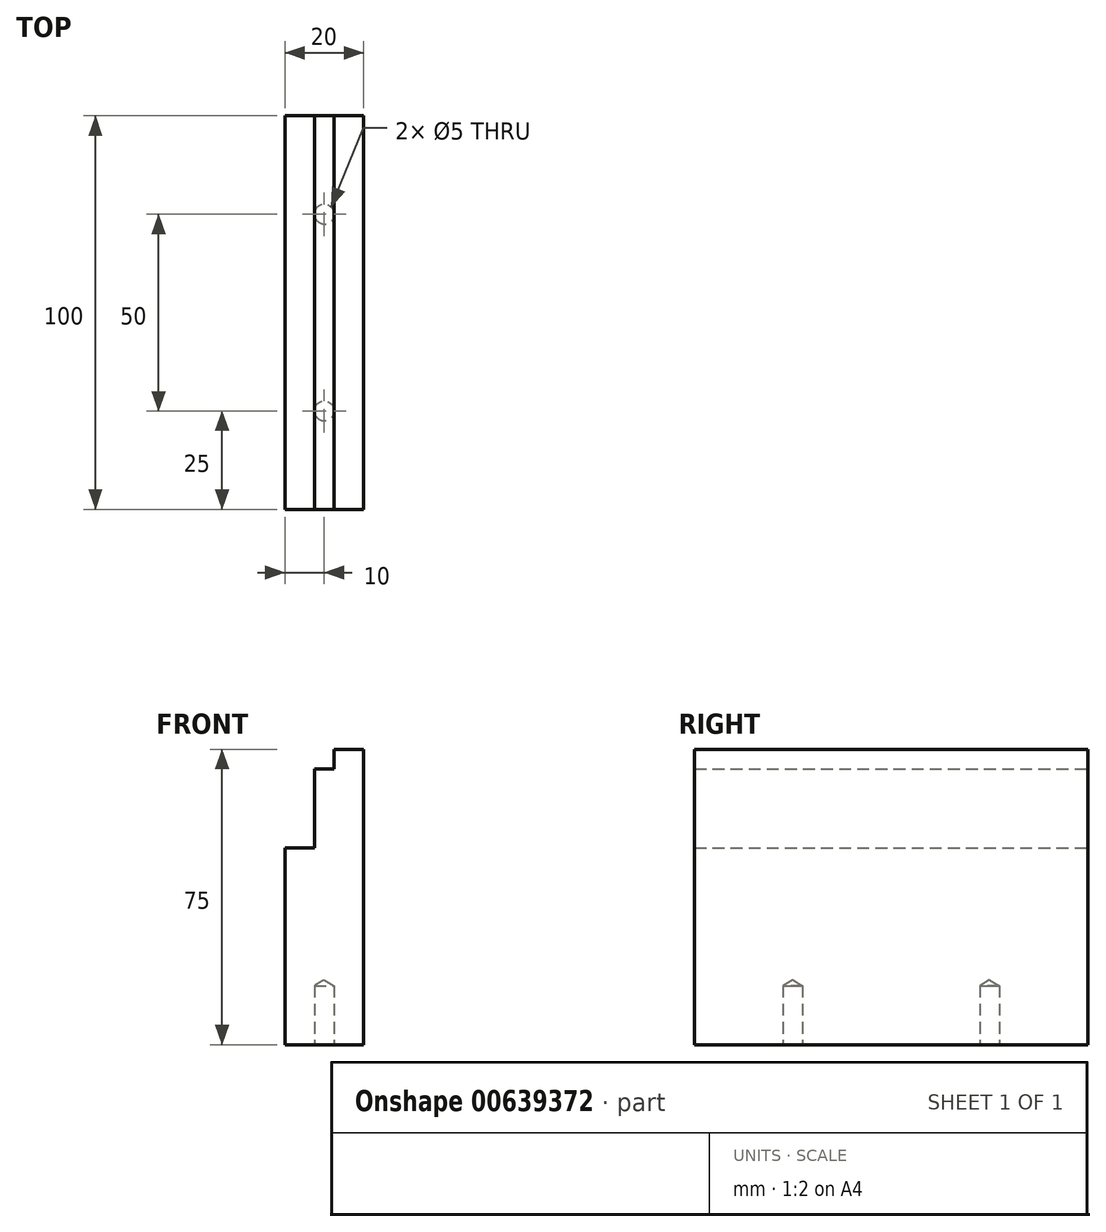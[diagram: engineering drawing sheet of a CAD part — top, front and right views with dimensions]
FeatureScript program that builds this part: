
annotation { "Feature Type Name" : "Feature", "Feature Type Description" : "" }
export const myFeature = defineFeature(function(context is Context, id is Id, definition is map)
    precondition{}
    {
        {
            var Q0;
            Q0=qCreatedBy(makeId("Front.planeOp"),FACE);
            var sketch = newSketch(context, id + "F0", { "sketchPlane" : qUnion([Q0])});
            skLineSegment(sketch, "E0.top", {"start": v(130, 75) * mm, "end": v(137.5, 75) * mm});
            skLineSegment(sketch, "E0.left", {"start": v(117.5, 0) * mm, "end": v(117.5, 50) * mm});
            skLineSegment(sketch, "E0.right", {"start": v(137.5, 0) * mm, "end": v(137.5, 75) * mm});
            skLineSegment(sketch, "E1", {"start": v(130, 75) * mm, "end": v(130, 70) * mm});
            skLineSegment(sketch, "E2", {"start": v(130, 70) * mm, "end": v(125, 70) * mm});
            skLineSegment(sketch, "E3", {"start": v(125, 70) * mm, "end": v(125, 50) * mm});
            skLineSegment(sketch, "E4", {"start": v(125, 50) * mm, "end": v(117.5, 50) * mm});
            skLineSegment(sketch, "E5", {"start": v(117.5, 0) * mm, "end": v(137.5, 0) * mm});
            skPoint(sketch, "E6", {"position": v(127.5, 0) * mm});
            skSolve(sketch);
        }
        {
            var Q0;
            Q0=makeQuery(id+"F0.imprint","IMPRINT",FACE,{"disambiguationData":[TD([[makeQuery(id+"F0.imprint","IMPRINT",EDGE,{"derivedFrom":sQuery(id+"F0.wireOp",EDGE,"E0.top")}),-1.0]])]});
            extrude(context, id + "F1", {"entities" : qUnion([Q0]), "depth" : 100 * mm, "offsetDistance" : 25 * mm});
        }
        {
            var Q0;
            Q0=makeQuery(id+"F1.opExtrude","SWEPT_FACE",FACE,{"disambiguationData":[OSD([sQuery(id+"F0.wireOp",EDGE,"E5")])]});
            var sketch = newSketch(context, id + "F2", { "sketchPlane" : qUnion([Q0])});
            skCircle(sketch, "E7", {"center": v(127.5, 75) * mm, "radius": 3 * mm});
            skPoint(sketch, "E7.centerSnap0", {"position": v(127.5, 100) * mm});
            skCircle(sketch, "E8", {"center": v(127.5, 25) * mm, "radius": 3 * mm});
            skSolve(sketch);
        }
        {
            var Q0;
            Q0=sQuery(id+"F2.wireOp",VERTEX,"E7.center");
            var Q1;
            Q1=sQuery(id+"F2.wireOp",VERTEX,"E8.center");
            var Q2;
            Q2=makeQuery(id+"F1.opExtrude","SWEPT_BODY",BODY,{"disambiguationData":[OSD([sQuery(id+"F0.wireOp",EDGE,"E0.top"),sQuery(id+"F0.wireOp",EDGE,"E0.left"),sQuery(id+"F0.wireOp",EDGE,"E0.right"),sQuery(id+"F0.wireOp",EDGE,"E1"),sQuery(id+"F0.wireOp",EDGE,"E2"),sQuery(id+"F0.wireOp",EDGE,"E3"),sQuery(id+"F0.wireOp",EDGE,"E4"),sQuery(id+"F0.wireOp",EDGE,"E5")])]});
            hole(context, id + "F3", {"style" : HoleStyle.SIMPLE, "endStyle" : HoleEndStyle.BLIND, "standardTappedOrClearance" : lookupTablePath({ "standard" : "ISO", "engagement" : "75%", "pitch" : "1 mm", "size" : "M6", "type" : "Tapped" }), "standardBlindInLast" : lookupTablePath({ "standard" : "ISO", "engagement" : "75%", "pitch" : "1 mm", "size" : "M6", "type" : "Tapped" }), "holeDiameter" : 5 * mm, "majorDiameter" : 6 * mm, "showTappedDepth" : true, "holeDepth" : 15 * mm, "isTappedThrough" : true, "tappedDepth" : 12 * mm, "tapClearance" : 3, "locations" : qUnion([Q0, Q1]), "scope" : qUnion([Q2])});
        }
    });
